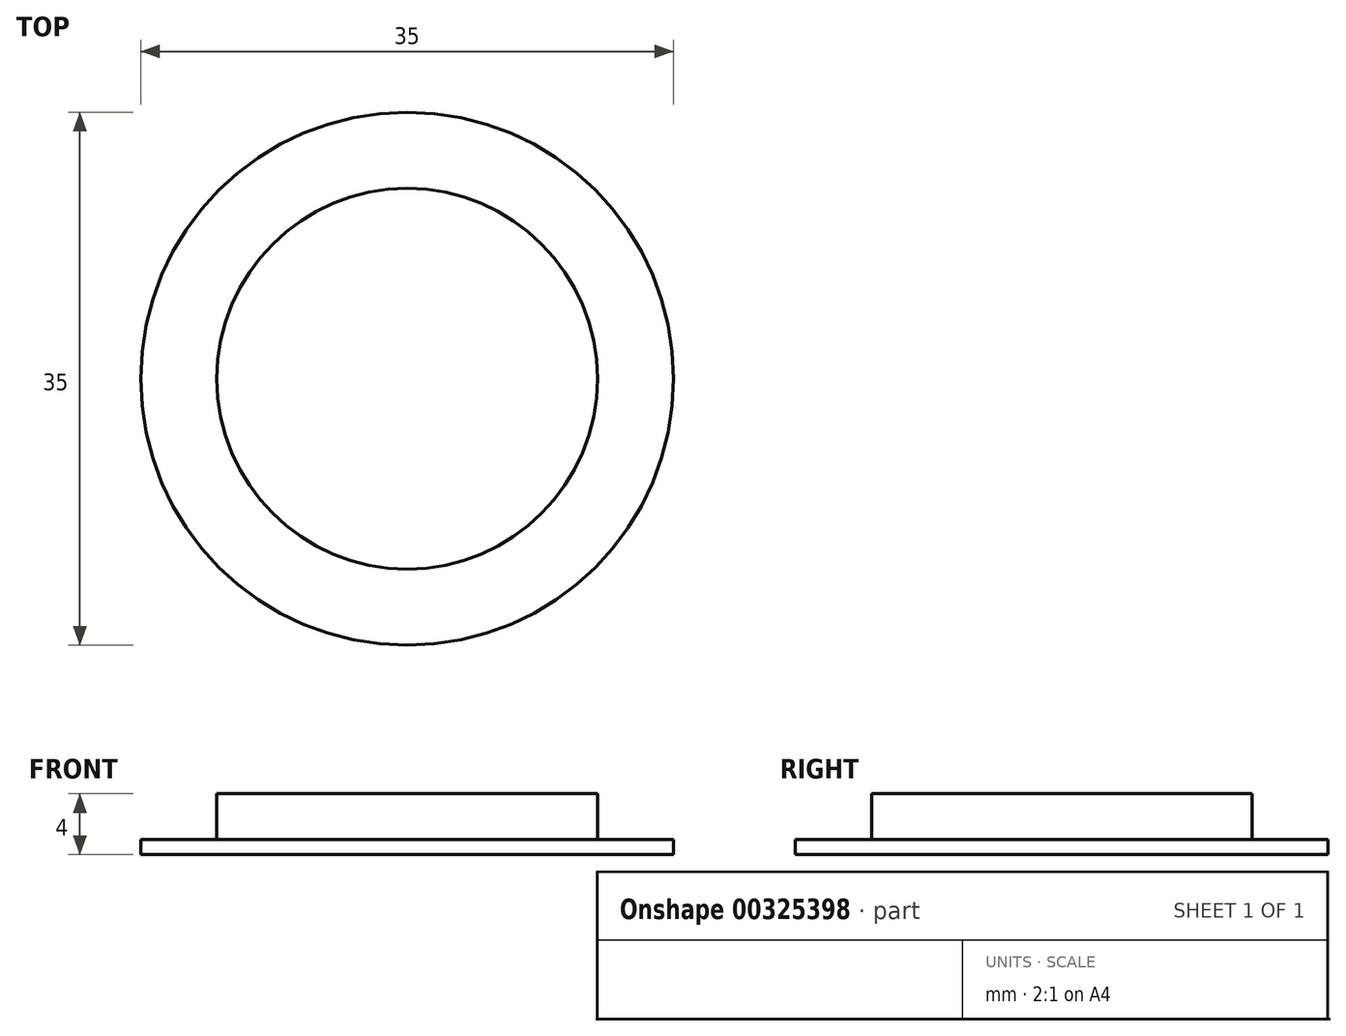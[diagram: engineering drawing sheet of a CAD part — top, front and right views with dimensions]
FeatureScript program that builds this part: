
annotation { "Feature Type Name" : "Feature", "Feature Type Description" : "" }
export const myFeature = defineFeature(function(context is Context, id is Id, definition is map)
    precondition{}
    {
        {
            var Q0;
            Q0=qCreatedBy(makeId("Top.planeOp"),FACE);
            var sketch = newSketch(context, id + "F0", { "sketchPlane" : qUnion([Q0])});
            skCircle(sketch, "E0", {"center": v(0, 0) * mm, "radius": 12.5 * mm});
            skCircle(sketch, "E1.0", {"center": v(0, 0) * mm, "radius": 17.5 * mm});
            skSolve(sketch);
        }
        {
            var Q0;
            Q0=qCreatedBy(makeId("Top.planeOp"),FACE);
            var sketch = newSketch(context, id + "F1", { "sketchPlane" : qUnion([Q0])});
            skCircle(sketch, "E2", {"center": v(0, 0) * mm, "radius": 12.5 * mm});
            skCircle(sketch, "E3.0", {"center": v(0, 0) * mm, "radius": 17.5 * mm});
            skSolve(sketch);
        }
        {
            var Q0;
            Q0=makeQuery(id+"F0.imprint","IMPRINT",FACE,{"disambiguationData":[TD([[makeQuery(id+"F0.imprint","IMPRINT",EDGE,{"derivedFrom":sQuery(id+"F0.wireOp",EDGE,"E0")}),1.0]])]});
            extrude(context, id + "F2", {"entities" : qUnion([Q0]), "depth" : 4 * mm});
        }
        {
            var Q0;
            Q0=makeQuery(id+"F1.imprint","IMPRINT",FACE,{"disambiguationData":[TD([[makeQuery(id+"F1.imprint","IMPRINT",EDGE,{"derivedFrom":sQuery(id+"F1.wireOp",EDGE,"E2")}),-1.0]])]});
            extrude(context, id + "F3", {"entities" : qUnion([Q0]), "operationType" : NewBodyOperationType.ADD, "depth" : 1 * mm});
        }
    });
